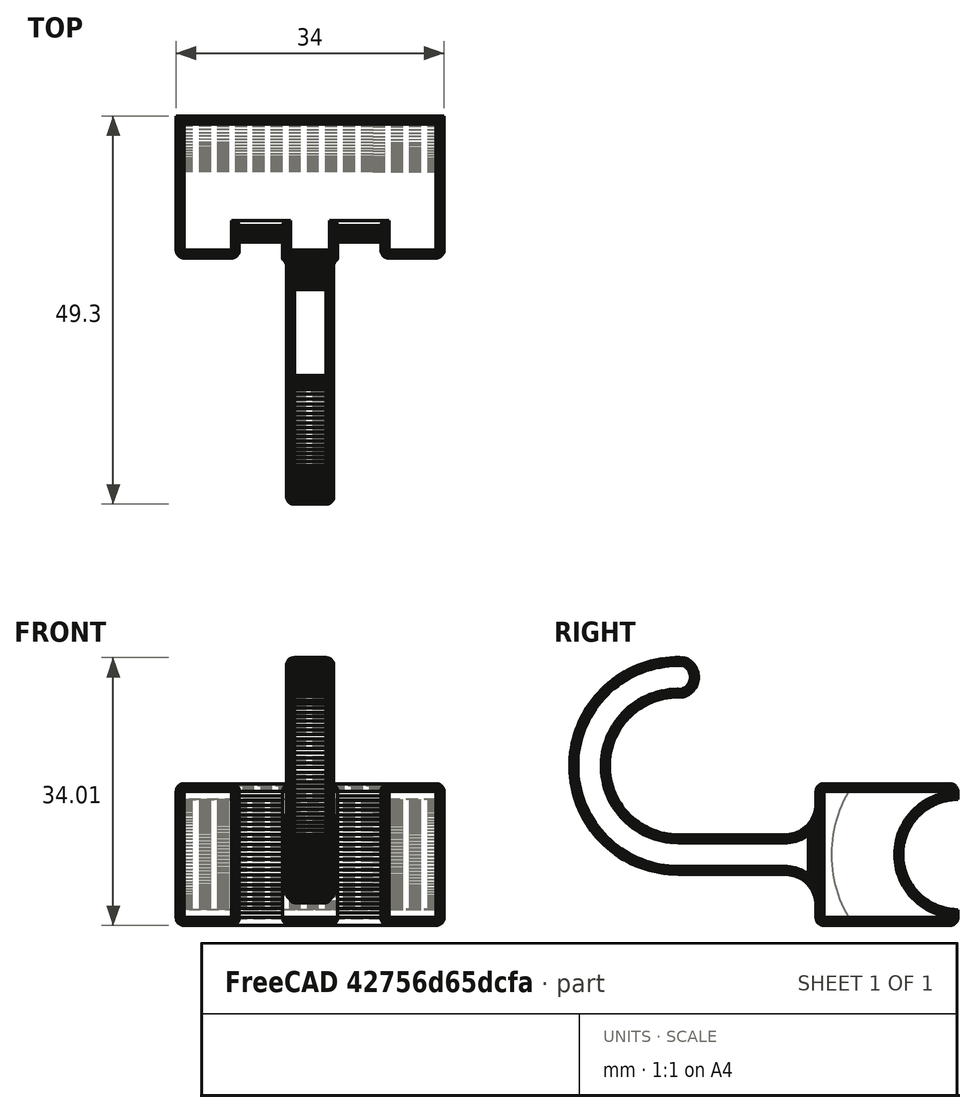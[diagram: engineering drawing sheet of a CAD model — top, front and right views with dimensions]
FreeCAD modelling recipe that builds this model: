
FCSTD DOCUMENT  (FreeCAD 1.0R39109 (Git))
Label: 01_ZipTieHook
License: All rights reserved
LicenseURL: https://en.wikipedia.org/wiki/All_rights_reserved
objects: Part::Feature×1, PartDesign::FeatureBase×1, Sketcher::SketchObject×1, PartDesign::Body×1
note: 6 computed .brp shape members not serialized (recipe doc carries the construction recipe); baked Part::Feature solids carry a one-line shape summary decoded from their .brp

FEATURE [Part::Feature] Zip_Tie_Hook005_solid  label="Zip_Tie_Hook005 (Solid)"
  shape: bbox 34 x 49.3 x 34.01 mm, 13742 faces (baked)
FEATURE [PartDesign::FeatureBase] BaseFeature
  BaseFeature = -> Zip_Tie_Hook005_solid
  Suppressed = false
FEATURE [Sketcher::SketchObject] Sketch
  ArcFitTolerance = 1e-06
  AttachmentSupport = -> [BaseFeature]
  FullyConstrained = true
  MakeInternals = false
  MapMode = 5
  Placement = pos=(17,0,0) rot=(0.57735,0.57735,0.57735;2.0944rad)
FEATURE [PartDesign::Body] Body
  AllowCompound = false
  BaseFeature = -> Zip_Tie_Hook005_solid
  Group = -> [BaseFeature,Sketch]
  Origin = -> Origin
  Tip = -> BaseFeature
